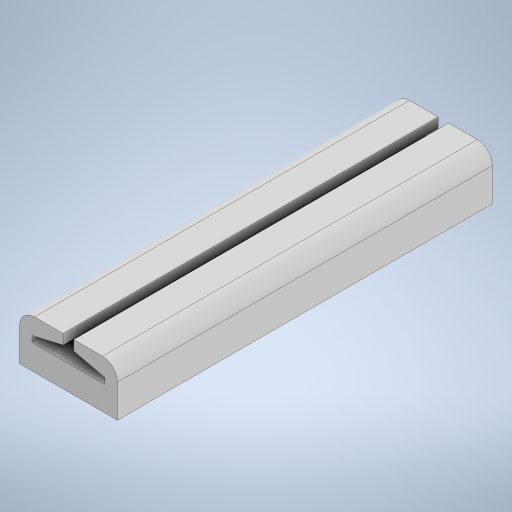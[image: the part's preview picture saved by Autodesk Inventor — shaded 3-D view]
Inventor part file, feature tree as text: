
AUTODESK INVENTOR PART (.ipt)
format: ipt  version: 2023 (Build 270158030, 158C)  size: 269,312 bytes
history: native  units: in
note: dims shown in document units (in); Inventor stores cm internally (conversion verified against a paired STEP export)
features: extrude x1, sketch x1
ambient origin geometry x8: Origin, YZ Plane, XZ Plane, XY Plane, X Axis, Y Axis, Z Axis, Center Point
bodies: Solid1 (feature_tree)
feature tree (2):
  extrude  "Extrusion1"  Depth=0.03in
  sketch  "Sketch1"  dims[d3=0.026in d4=0.0104in d5=1.1475in d6=0.0833in d7=0.0417in d9=0.0893in d10=0.01in d11=0.75in d12=0.0in d13=0.05in d14=0.02in d15=0.025in d16=0.025in d17=0.03in]
